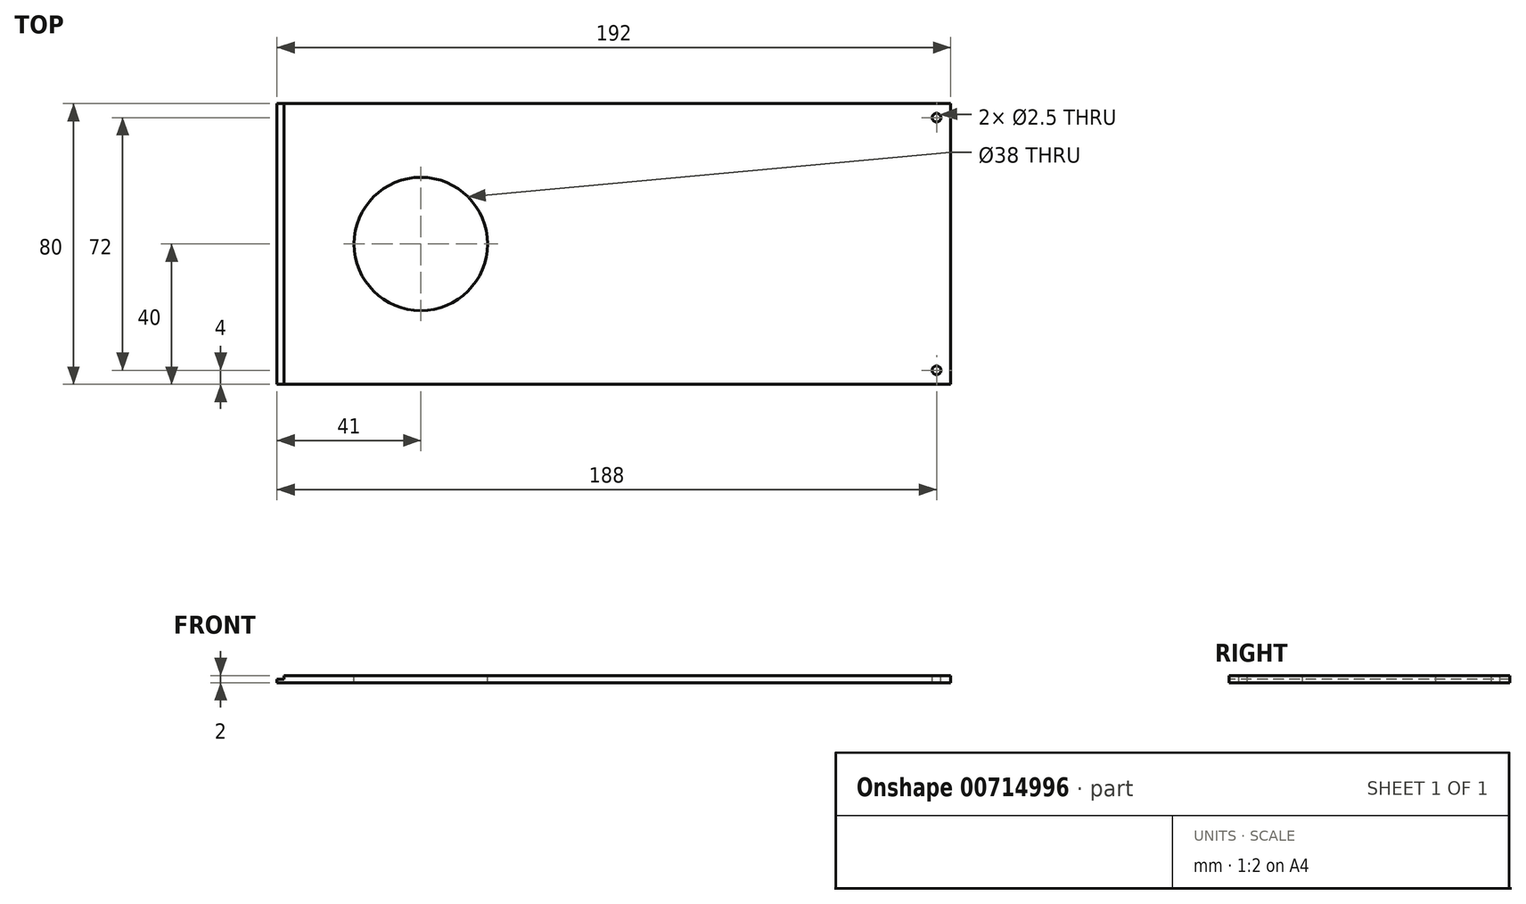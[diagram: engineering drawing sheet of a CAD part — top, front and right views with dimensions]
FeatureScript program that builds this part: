
annotation { "Feature Type Name" : "Feature", "Feature Type Description" : "" }
export const myFeature = defineFeature(function(context is Context, id is Id, definition is map)
    precondition{}
    {
        {
            var Q0;
            Q0=qCreatedBy(makeId("Top.planeOp"),FACE);
            var sketch = newSketch(context, id + "F0", { "sketchPlane" : qUnion([Q0])});
            skLineSegment(sketch, "E0.bottom", {"start": v(96, 40) * mm, "end": v(-96, 40) * mm});
            skLineSegment(sketch, "E0.top", {"start": v(96, -40) * mm, "end": v(-96, -40) * mm});
            skLineSegment(sketch, "E0.left", {"start": v(96, 40) * mm, "end": v(96, -40) * mm});
            skLineSegment(sketch, "E0.right", {"start": v(-96, 40) * mm, "end": v(-96, -40) * mm});
            skPoint(sketch, "E0.middle", {"position": v(0, 0) * mm});
            skSolve(sketch);
        }
        {
            var Q0;
            Q0=makeQuery(id+"F0.imprint","IMPRINT",FACE,{"disambiguationData":[TD([[makeQuery(id+"F0.imprint","IMPRINT",EDGE,{"derivedFrom":sQuery(id+"F0.wireOp",EDGE,"E0.bottom")}),1.0]])]});
            extrude(context, id + "F1", {"entities" : qUnion([Q0]), "depth" : 2 * mm, "offsetDistance" : 25 * mm});
        }
        {
            var Q0;
            Q0=makeQuery(id+"F1.opExtrude","CAP_FACE",FACE,{"disambiguationData":[OSD([sQuery(id+"F0.wireOp",EDGE,"E0.bottom"),sQuery(id+"F0.wireOp",EDGE,"E0.top"),sQuery(id+"F0.wireOp",EDGE,"E0.left"),sQuery(id+"F0.wireOp",EDGE,"E0.right")])],"isStart":false});
            var sketch = newSketch(context, id + "F2", { "sketchPlane" : qUnion([Q0])});
            skLineSegment(sketch, "E1.bottom", {"start": v(-96, 40) * mm, "end": v(-94, 40) * mm});
            skLineSegment(sketch, "E1.top", {"start": v(-96, -40) * mm, "end": v(-94, -40) * mm});
            skLineSegment(sketch, "E1.left", {"start": v(-96, 40) * mm, "end": v(-96, -40) * mm});
            skLineSegment(sketch, "E1.right", {"start": v(-94, 40) * mm, "end": v(-94, -40) * mm});
            skSolve(sketch);
        }
        {
            var Q0;
            Q0 = qSketchRegion(id + "F2", true);
            extrude(context, id + "F3", {"entities" : qUnion([Q0]), "operationType" : NewBodyOperationType.REMOVE, "oppositeDirection" : true, "depth" : 1 * mm, "offsetDistance" : 25 * mm});
        }
        {
            var Q0;
            Q0=makeQuery(id+"F1.opExtrude","CAP_FACE",FACE,{"disambiguationData":[OSD([sQuery(id+"F0.wireOp",EDGE,"E0.bottom"),sQuery(id+"F0.wireOp",EDGE,"E0.top"),sQuery(id+"F0.wireOp",EDGE,"E0.left"),sQuery(id+"F0.wireOp",EDGE,"E0.right")])],"isStart":false});
            var sketch = newSketch(context, id + "F4", { "sketchPlane" : qUnion([Q0])});
            skLineSegment(sketch, "E2.bottom", {"start": v(96, -40) * mm, "end": v(92, -40) * mm, "construction": true});
            skLineSegment(sketch, "E2.top", {"start": v(96, -36) * mm, "end": v(92, -36) * mm, "construction": true});
            skLineSegment(sketch, "E2.left", {"start": v(96, -40) * mm, "end": v(96, -36) * mm, "construction": true});
            skLineSegment(sketch, "E2.right", {"start": v(92, -40) * mm, "end": v(92, -36) * mm, "construction": true});
            skLineSegment(sketch, "E3.bottom", {"start": v(96, 40) * mm, "end": v(92, 40) * mm, "construction": true});
            skLineSegment(sketch, "E3.top", {"start": v(96, 36) * mm, "end": v(92, 36) * mm, "construction": true});
            skLineSegment(sketch, "E3.left", {"start": v(96, 40) * mm, "end": v(96, 36) * mm, "construction": true});
            skLineSegment(sketch, "E3.right", {"start": v(92, 40) * mm, "end": v(92, 36) * mm, "construction": true});
            skSolve(sketch);
        }
        {
            var Q0;
            Q0=sQuery(id+"F4.wireOp",VERTEX,"E3.top.end");
            var Q1;
            Q1=sQuery(id+"F4.wireOp",VERTEX,"E2.top.end");
            var Q2;
            Q2=makeQuery(id+"F1.opExtrude","SWEPT_BODY",BODY,{"disambiguationData":[OSD([sQuery(id+"F0.wireOp",EDGE,"E0.bottom"),sQuery(id+"F0.wireOp",EDGE,"E0.top"),sQuery(id+"F0.wireOp",EDGE,"E0.left"),sQuery(id+"F0.wireOp",EDGE,"E0.right")])]});
            hole(context, id + "F5", {"style" : HoleStyle.SIMPLE, "endStyle" : HoleEndStyle.THROUGH, "holeDiameter" : 2.5 * mm, "majorDiameter" : 5 * mm, "isTappedThrough" : true, "tappedDepth" : 12 * mm, "tapClearance" : 3, "startFromSketch" : true, "locations" : qUnion([Q0, Q1]), "scope" : qUnion([Q2])});
        }
        {
            var Q0;
            Q0=makeQuery(id+"F1.opExtrude","CAP_FACE",FACE,{"disambiguationData":[OSD([sQuery(id+"F0.wireOp",EDGE,"E0.bottom"),sQuery(id+"F0.wireOp",EDGE,"E0.top"),sQuery(id+"F0.wireOp",EDGE,"E0.left"),sQuery(id+"F0.wireOp",EDGE,"E0.right")])],"isStart":false});
            var sketch = newSketch(context, id + "F6", { "sketchPlane" : qUnion([Q0])});
            skLineSegment(sketch, "E4.bottom", {"start": v(-94, 40) * mm, "end": v(-55, 40) * mm, "construction": true});
            skLineSegment(sketch, "E4.top", {"start": v(-94, -40) * mm, "end": v(-55, -40) * mm, "construction": true});
            skLineSegment(sketch, "E4.left", {"start": v(-94, 40) * mm, "end": v(-94, -40) * mm, "construction": true});
            skLineSegment(sketch, "E4.right", {"start": v(-55, 40) * mm, "end": v(-55, -40) * mm, "construction": true});
            skLineSegment(sketch, "E5", {"start": v(-55, 40) * mm, "end": v(-55, 0) * mm, "construction": true});
            skSolve(sketch);
        }
        {
            var Q0;
            Q0=sQuery(id+"F6.wireOp",VERTEX,"E5.end");
            var Q1;
            Q1=makeQuery(id+"F1.opExtrude","SWEPT_BODY",BODY,{"disambiguationData":[OSD([sQuery(id+"F0.wireOp",EDGE,"E0.bottom"),sQuery(id+"F0.wireOp",EDGE,"E0.top"),sQuery(id+"F0.wireOp",EDGE,"E0.left"),sQuery(id+"F0.wireOp",EDGE,"E0.right")])]});
            hole(context, id + "F7", {"style" : HoleStyle.SIMPLE, "endStyle" : HoleEndStyle.THROUGH, "holeDiameter" : 38 * mm, "majorDiameter" : 5 * mm, "isTappedThrough" : true, "tappedDepth" : 12 * mm, "tapClearance" : 3, "startFromSketch" : true, "locations" : qUnion([Q0]), "scope" : qUnion([Q1])});
        }
    });
